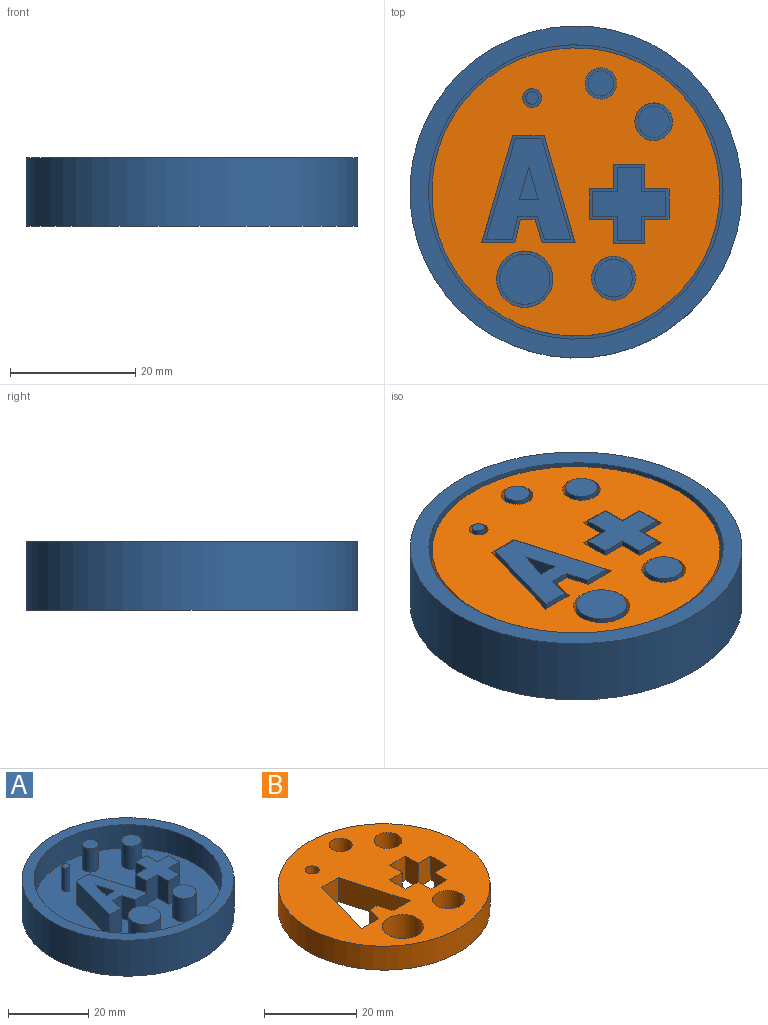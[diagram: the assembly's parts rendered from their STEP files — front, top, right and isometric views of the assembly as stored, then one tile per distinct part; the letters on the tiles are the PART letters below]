
ASSEMBLY  parts=2 mates=1
PART A: 41 faces, bbox 53x53x11 mm
  f0: plane 53x53mm, normal (0,0,1), area 471.2mm2, adj f1,f26
  f1: cylinder r=26.5mm len=53mm, axis (0,0,1), area 1831.5mm2, adj f0,f2
  f2: plane 53x53mm, normal (0,0,-1), area 2206.2mm2, adj f1
  f3: plane 16.11x7.11mm, normal (-0.96,0.28,0), area 119.2mm2, adj f4,f28,f29,f36
  f4: plane 7.11x4.28mm, normal (0,1,0), area 30.4mm2, adj f3,f5,f29,f36
  f5: plane 16.11x7.11mm, normal (0.96,0.28,0), area 119.2mm2, adj f4,f6,f29,f36
  f6: plane 7.11x4.24mm, normal (0,-1,0), area 30.2mm2, adj f5,f7,f29,f36
  f7: plane 7.11x3.76mm, normal (-0.96,-0.28,0), area 27.9mm2, adj f6,f8,f29,f36
  f8: plane 7.11x3.14mm, normal (0,-1,0), area 22.3mm2, adj f7,f9,f29,f36
  f9: plane 7.11x3.76mm, normal (0.98,-0.22,0), area 27.4mm2, adj f8,f28,f29,f36
  f10: plane 7.11x3.9mm, normal (-1,0,0), area 27.7mm2, adj f11,f27,f29,f30
  f11: plane 7.11x3.9mm, normal (0,1,0), area 27.7mm2, adj f10,f12,f29,f30
  f12: plane 7.11x3.9mm, normal (1,0,0), area 27.7mm2, adj f11,f13,f29,f30
  f13: plane 7.11x3.9mm, normal (0,1,0), area 27.7mm2, adj f12,f14,f29,f30
  f14: plane 7.11x3.9mm, normal (1,0,0), area 27.7mm2, adj f13,f15,f29,f30
  f15: plane 7.11x3.9mm, normal (0,-1,0), area 27.7mm2, adj f14,f16,f29,f30
  f16: plane 7.11x3.9mm, normal (1,0,0), area 27.7mm2, adj f15,f17,f29,f30
  f17: plane 7.11x3.9mm, normal (0,-1,0), area 27.7mm2, adj f16,f18,f29,f30
  f18: plane 7.11x3.9mm, normal (-1,0,0), area 27.7mm2, adj f17,f19,f29,f30
  f19: plane 7.11x3.9mm, normal (0,-1,0), area 27.7mm2, adj f18,f20,f29,f30
  f20: plane 7.11x3.9mm, normal (-1,0,0), area 27.7mm2, adj f19,f27,f29,f30
  f21: cylinder r=4mm len=8mm, axis (0,0,1), area 178.7mm2, adj f29,f35
  f22: cylinder r=3mm len=7.11mm, axis (0,0,1), area 134.1mm2, adj f29,f34
  f23: cylinder r=2.5mm len=7.11mm, axis (0,0,1), area 111.7mm2, adj f29,f33
  f24: cylinder r=2mm len=7.11mm, axis (0,0,1), area 89.4mm2, adj f29,f32
  f25: cylinder r=1mm len=7.11mm, axis (0,0,1), area 44.7mm2, adj f29,f31
  f26: cylinder r=23.5mm len=47mm, axis (0,0,1), area 1050.1mm2, adj f0,f29
  f27: plane 7.11x3.9mm, normal (0,1,0), area 27.7mm2, adj f10,f20,f29,f30
  f28: plane 7.11x4.24mm, normal (0,-1,0), area 30.2mm2, adj f3,f9,f29,f36
  f29: plane 47x47mm, normal (0,0,1), area 1416.8mm2, adj f3,f4,f5,f6,f7,f8,f9,f10
  f30: plane 11.69x11.69mm, normal (0,0,1), area 75.9mm2, adj f10,f11,f12,f13,f14,f15,f16,f17
  f31: plane 2x2mm, normal (0,0,1), area 3.1mm2, adj f25
  f32: plane 4x4mm, normal (0,0,1), area 12.6mm2, adj f24
  f33: plane 5x5mm, normal (0,0,1), area 19.6mm2, adj f23
  f34: plane 6x6mm, normal (0,0,1), area 28.3mm2, adj f22
  f35: plane 8x8mm, normal (0,0,1), area 50.3mm2, adj f21
  f36: plane 16.11x13.58mm, normal (0,0,1), area 120.5mm2, adj f3,f4,f5,f6,f7,f8,f9,f28
  f37: plane 7.11x5.19mm, normal (-0.96,-0.28,0), area 38.4mm2, adj f36,f38,f39,f40
  f38: plane 7.11x5.19mm, normal (0.96,-0.28,0), area 38.4mm2, adj f36,f37,f39,f40
  f39: plane 7.11x3.04mm, normal (0,1,0), area 21.6mm2, adj f36,f37,f38,f40
  f40: plane 5.19x3.04mm, normal (0,0,1), area 7.9mm2, adj f37,f38,f39
PART B: 28 faces, bbox 46x46x6.4 mm
  f0: plane 17.11x6.35mm, normal (0.96,-0.28,0), area 113.1mm2, adj f1,f23,f26,f27
  f1: plane 6.35x5.03mm, normal (0,-1,0), area 32mm2, adj f0,f2,f26,f27
  f2: plane 17.11x6.35mm, normal (-0.96,-0.28,0), area 113.1mm2, adj f1,f3,f26,f27
  f3: plane 6.35x5.28mm, normal (0,1,0), area 33.5mm2, adj f2,f4,f26,f27
  f4: plane 6.35x3.76mm, normal (0.96,0.28,0), area 24.9mm2, adj f3,f5,f26,f27
  f5: plane 6.35x2.36mm, normal (0,1,0), area 15mm2, adj f4,f6,f26,f27
  f6: plane 6.35x3.76mm, normal (-0.98,0.22,0), area 24.5mm2, adj f5,f23,f26,f27
  f7: plane 6.35x3.9mm, normal (1,0,0), area 24.7mm2, adj f8,f24,f26,f27
  f8: plane 6.35x4.9mm, normal (0,-1,0), area 31.1mm2, adj f7,f9,f26,f27
  f9: plane 6.35x3.9mm, normal (-1,0,0), area 24.7mm2, adj f8,f10,f26,f27
  f10: plane 6.35x3.9mm, normal (0,-1,0), area 24.7mm2, adj f9,f11,f26,f27
  f11: plane 6.35x4.9mm, normal (-1,0,0), area 31.1mm2, adj f10,f12,f26,f27
  f12: plane 6.35x3.9mm, normal (0,1,0), area 24.7mm2, adj f11,f13,f26,f27
  f13: plane 6.35x3.9mm, normal (-1,0,0), area 24.7mm2, adj f12,f14,f26,f27
  f14: plane 6.35x4.9mm, normal (0,1,0), area 31.1mm2, adj f13,f15,f26,f27
  f15: plane 6.35x3.9mm, normal (1,0,0), area 24.7mm2, adj f14,f16,f26,f27
  f16: plane 6.35x3.9mm, normal (0,1,0), area 24.7mm2, adj f15,f17,f26,f27
  f17: plane 6.35x4.9mm, normal (1,0,0), area 31.1mm2, adj f16,f24,f26,f27
  f18: cylinder r=1.5mm len=6.35mm, axis (0,0,-1), area 59.8mm2, adj f26,f27
  f19: cylinder r=2.5mm len=6.35mm, axis (0,0,-1), area 99.7mm2, adj f26,f27
  f20: cylinder r=3mm len=6.35mm, axis (0,0,-1), area 119.7mm2, adj f26,f27
  f21: cylinder r=4.5mm len=9mm, axis (0,0,-1), area 179.5mm2, adj f26,f27
  f22: cylinder r=3.5mm len=7mm, axis (0,0,-1), area 139.6mm2, adj f26,f27
  f23: plane 6.35x5.3mm, normal (0,1,0), area 33.7mm2, adj f0,f6,f26,f27
  f24: plane 6.35x3.9mm, normal (0,-1,0), area 24.7mm2, adj f7,f17,f26,f27
  f25: cylinder r=23mm len=46mm, axis (0,0,-1), area 917.7mm2, adj f26,f27
  f26: plane 46x46mm, normal (0,0,1), area 1246.5mm2, adj f0,f1,f2,f3,f4,f5,f6,f7
  f27: plane 46x46mm, normal (0,0,-1), area 1246.5mm2, adj f0,f1,f2,f3,f4,f5,f6,f7
PLACE A t=(77.95,-40.78,20.03)mm
PLACE B t=(79.2,-41.79,13.3)mm
MATE fastened B.f25 <-> A.f26  axis (0,0,-1) through (77.95,-40.78,16.47)mm
